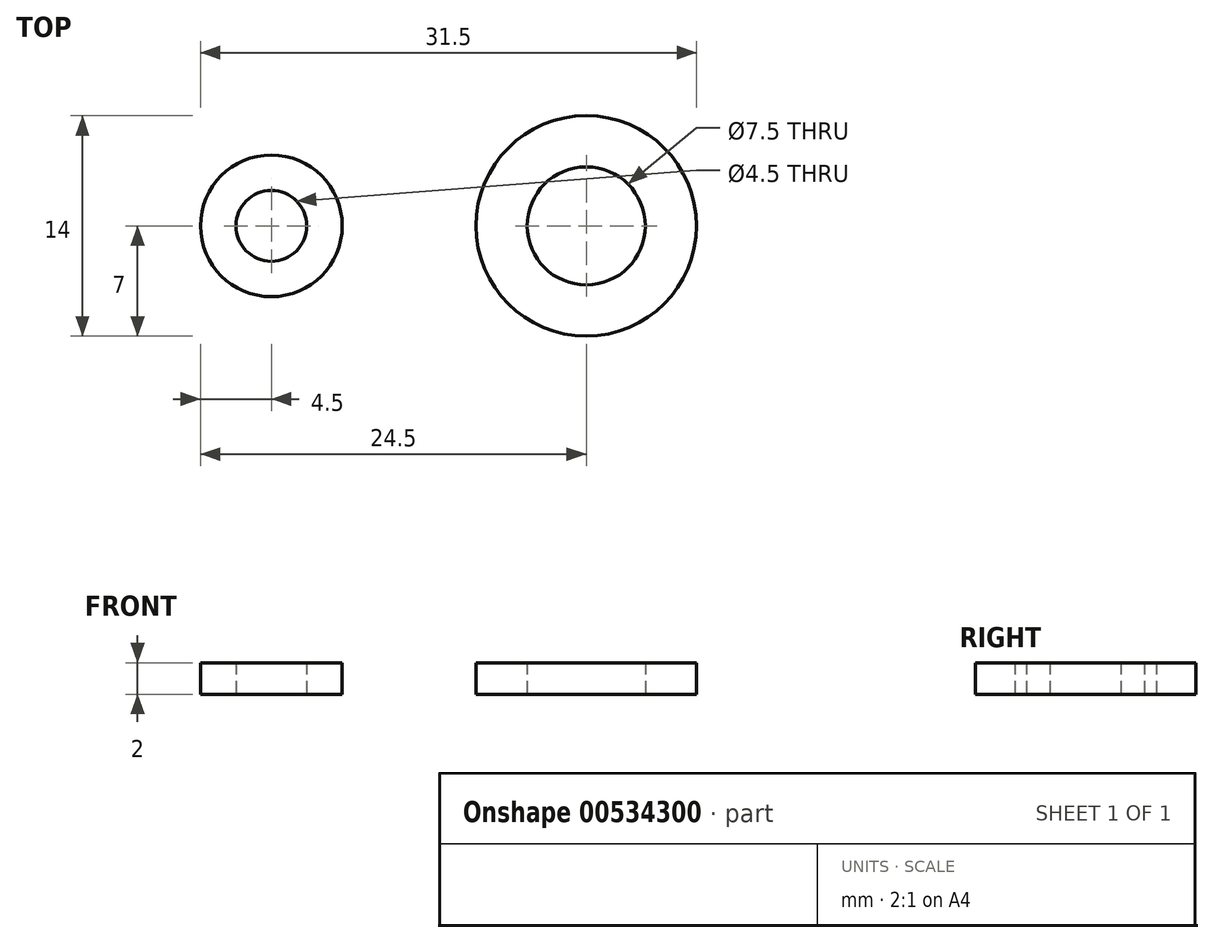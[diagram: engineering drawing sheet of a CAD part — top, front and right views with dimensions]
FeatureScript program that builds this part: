
annotation { "Feature Type Name" : "Feature", "Feature Type Description" : "" }
export const myFeature = defineFeature(function(context is Context, id is Id, definition is map)
    precondition{}
    {
        {
            var Q0;
            Q0=qCreatedBy(makeId("Top.planeOp"),FACE);
            var sketch = newSketch(context, id + "F0", { "sketchPlane" : qUnion([Q0])});
            skCircle(sketch, "E0", {"center": v(0, 0) * mm, "radius": 2.25 * mm});
            skCircle(sketch, "E1", {"center": v(0, 0) * mm, "radius": 4.5 * mm});
            skSolve(sketch);
        }
        {
            var Q0;
            Q0=makeQuery(id+"F0.imprint","IMPRINT",FACE,{"disambiguationData":[TD([[makeQuery(id+"F0.imprint","IMPRINT",EDGE,{"derivedFrom":sQuery(id+"F0.wireOp",EDGE,"E0")}),-1.0]])]});
            extrude(context, id + "F1", {"entities" : qUnion([Q0]), "depth" : 2 * mm, "offsetDistance" : 25 * mm});
        }
        {
            var Q0;
            Q0=qCreatedBy(makeId("Top.planeOp"),FACE);
            var sketch = newSketch(context, id + "F2", { "sketchPlane" : qUnion([Q0])});
            skLineSegment(sketch, "E2", {"start": v(0, 0) * mm, "end": v(20, 0) * mm, "construction": true});
            skCircle(sketch, "E3", {"center": v(20, 0) * mm, "radius": 3.75 * mm});
            skCircle(sketch, "E4", {"center": v(20, 0) * mm, "radius": 7 * mm});
            skSolve(sketch);
        }
        {
            var Q0;
            Q0=makeQuery(id+"F2.imprint","IMPRINT",FACE,{"disambiguationData":[TD([[makeQuery(id+"F2.imprint","IMPRINT",EDGE,{"derivedFrom":sQuery(id+"F2.wireOp",EDGE,"E3")}),-1.0]])]});
            extrude(context, id + "F3", {"entities" : qUnion([Q0]), "depth" : 2 * mm, "offsetDistance" : 25 * mm});
        }
    });
